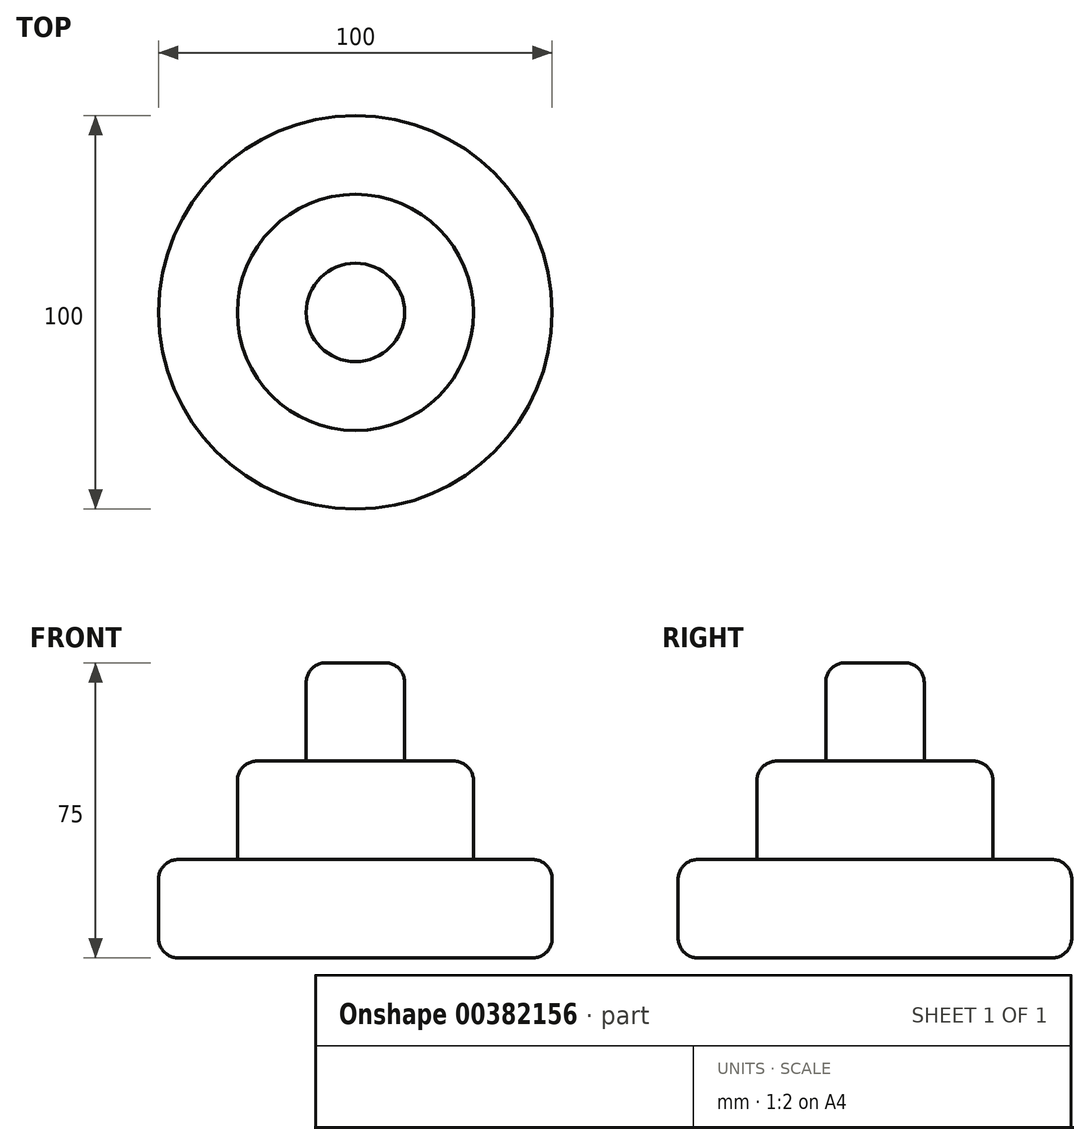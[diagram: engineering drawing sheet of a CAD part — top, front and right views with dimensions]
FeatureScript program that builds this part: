
annotation { "Feature Type Name" : "Feature", "Feature Type Description" : "" }
export const myFeature = defineFeature(function(context is Context, id is Id, definition is map)
    precondition{}
    {
        {
            var Q0;
            Q0=qCreatedBy(makeId("Top.planeOp"),FACE);
            var sketch = newSketch(context, id + "F0", { "sketchPlane" : qUnion([Q0])});
            skCircle(sketch, "E0", {"center": v(0, 0) * mm, "radius": 50 * mm});
            skSolve(sketch);
        }
        {
            var Q0;
            Q0=makeQuery(id+"F0.imprint","IMPRINT",FACE,{"disambiguationData":[TD([[makeQuery(id+"F0.imprint","IMPRINT",EDGE,{"derivedFrom":sQuery(id+"F0.wireOp",EDGE,"E0")}),1.0]])]});
            var sketch = newSketch(context, id + "F1", { "sketchPlane" : qUnion([Q0])});
            skCircle(sketch, "E1", {"center": v(0, 0) * mm, "radius": 30 * mm});
            skSolve(sketch);
        }
        {
            var Q0;
            Q0=makeQuery(id+"F1.imprint","IMPRINT",FACE,{"disambiguationData":[TD([[makeQuery(id+"F1.imprint","IMPRINT",EDGE,{"derivedFrom":sQuery(id+"F1.wireOp",EDGE,"E1")}),1.0]])]});
            extrude(context, id + "F2", {"entities" : qUnion([Q0]), "depth" : 25 * mm});
        }
        {
            var Q0;
            Q0=makeQuery(id+"F0.imprint","IMPRINT",FACE,{"disambiguationData":[TD([[makeQuery(id+"F0.imprint","IMPRINT",EDGE,{"derivedFrom":sQuery(id+"F0.wireOp",EDGE,"E0")}),1.0]])]});
            var Q1;
            Q1=makeQuery(id+"F2.opExtrude","CAP_FACE",FACE,{"disambiguationData":[OSD([sQuery(id+"F1.wireOp",EDGE,"E1")])],"isStart":false});
            extrude(context, id + "F3", {"entities" : qUnion([Q0, Q1]), "operationType" : NewBodyOperationType.ADD, "depth" : 25 * mm});
        }
        {
            var Q0;
            Q0=makeQuery(id+"F3.opExtrude","CAP_EDGE",EDGE,{"disambiguationData":[OSD([sQuery(id+"F0.wireOp",EDGE,"E0")])],"isStart":false});
            fillet(context, id + "F4", {"entities" : qUnion([Q0]), "radius" : 5 * mm, "tangentPropagation" : true, "allowEdgeOverflow" : false});
        }
        {
            var Q0;
            Q0=makeQuery(id+"F3.opExtrude","CAP_EDGE",EDGE,{"disambiguationData":[OSD([sQuery(id+"F1.wireOp",EDGE,"E1")])],"isStart":false});
            fillet(context, id + "F5", {"entities" : qUnion([Q0]), "radius" : 5 * mm, "tangentPropagation" : true, "allowEdgeOverflow" : false});
        }
        {
            var Q0;
            Q0=makeQuery(id+"F3.opExtrude","CAP_EDGE",EDGE,{"disambiguationData":[OSD([sQuery(id+"F0.wireOp",EDGE,"E0")])],"isStart":true});
            fillet(context, id + "F6", {"entities" : qUnion([Q0]), "radius" : 5 * mm, "tangentPropagation" : true, "allowEdgeOverflow" : false});
        }
        {
            var Q0;
            Q0=makeQuery(id+"F3.opExtrude","CAP_FACE",FACE,{"disambiguationData":[OSD([sQuery(id+"F1.wireOp",EDGE,"E1")])],"isStart":false});
            var sketch = newSketch(context, id + "F7", { "sketchPlane" : qUnion([Q0])});
            skCircle(sketch, "E2", {"center": v(0, 0) * mm, "radius": 12.5 * mm});
            skSolve(sketch);
        }
        {
            var Q0;
            Q0=makeQuery(id+"F7.imprint","IMPRINT",FACE,{"disambiguationData":[TD([[makeQuery(id+"F7.imprint","IMPRINT",EDGE,{"derivedFrom":sQuery(id+"F7.wireOp",EDGE,"E2")}),1.0]])]});
            extrude(context, id + "F8", {"entities" : qUnion([Q0]), "operationType" : NewBodyOperationType.ADD, "depth" : 25 * mm});
        }
        {
            var Q0;
            Q0=makeQuery(id+"F8.opExtrude","CAP_EDGE",EDGE,{"disambiguationData":[OSD([sQuery(id+"F7.wireOp",EDGE,"E2")])],"isStart":false});
            fillet(context, id + "F9", {"entities" : qUnion([Q0]), "radius" : 5 * mm, "tangentPropagation" : true, "allowEdgeOverflow" : false});
        }
    });
